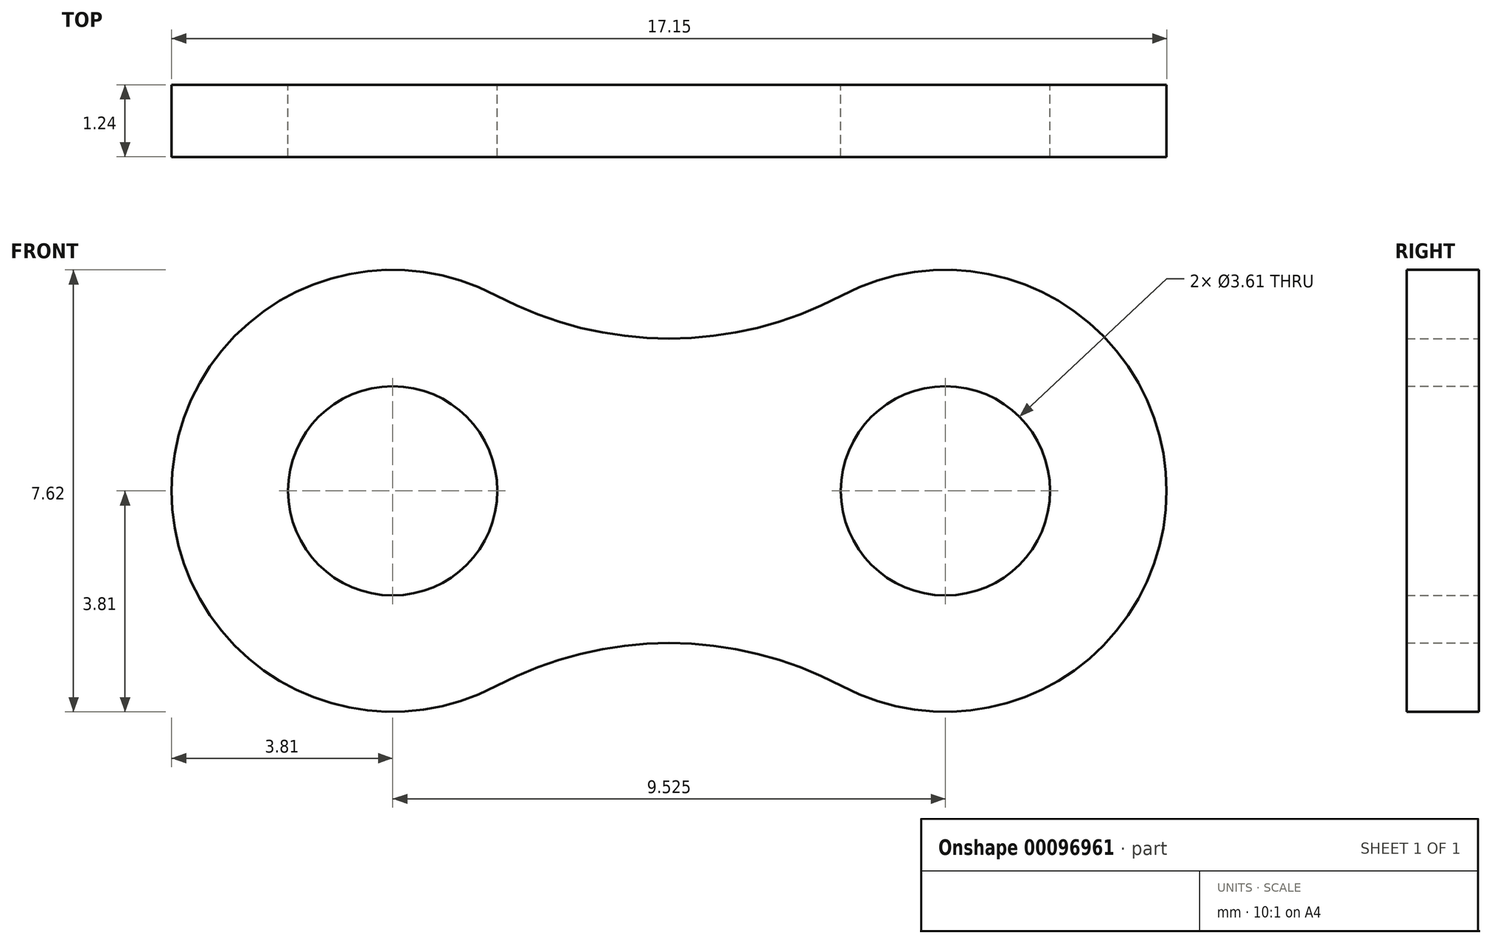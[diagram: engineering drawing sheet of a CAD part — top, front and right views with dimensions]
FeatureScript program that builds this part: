
annotation { "Feature Type Name" : "Feature", "Feature Type Description" : "" }
export const myFeature = defineFeature(function(context is Context, id is Id, definition is map)
    precondition{}
    {
        {
            var Q0;
            Q0=qCreatedBy(makeId("Front.planeOp"),FACE);
            var sketch = newSketch(context, id + "F0", { "sketchPlane" : qUnion([Q0])});
            skArc(sketch, "E0", {"start": v(1.79, 3.37) * mm, "mid": v(-3.81, 0) * mm, "end": v(1.79, -3.37) * mm});
            skArc(sketch, "E1", {"start": v(7.74, -3.37) * mm, "mid": v(13.33, 0) * mm, "end": v(7.74, 3.37) * mm});
            skLineSegment(sketch, "E2", {"start": v(0, 0) * mm, "end": v(9.53, 0) * mm, "construction": true});
            skLineSegment(sketch, "E3", {"start": v(4.76, 0) * mm, "end": v(4.76, 17.95) * mm, "construction": true});
            skArc(sketch, "E4", {"start": v(1.79, 3.37) * mm, "mid": v(4.76, 2.62) * mm, "end": v(7.74, 3.37) * mm});
            skArc(sketch, "E5.MirrorC", {"start": v(1.79, -3.37) * mm, "mid": v(4.76, -2.62) * mm, "end": v(7.74, -3.37) * mm});
            skCircle(sketch, "E6", {"center": v(0, 0) * mm, "radius": 1.8 * mm});
            skCircle(sketch, "E7", {"center": v(9.53, 0) * mm, "radius": 1.8 * mm});
            skSolve(sketch);
        }
        {
            var Q0;
            Q0 = qSketchRegion(id + "F0", true);
            extrude(context, id + "F1", {"entities" : qUnion([Q0]), "depth" : 1.24 * mm});
        }
    });
